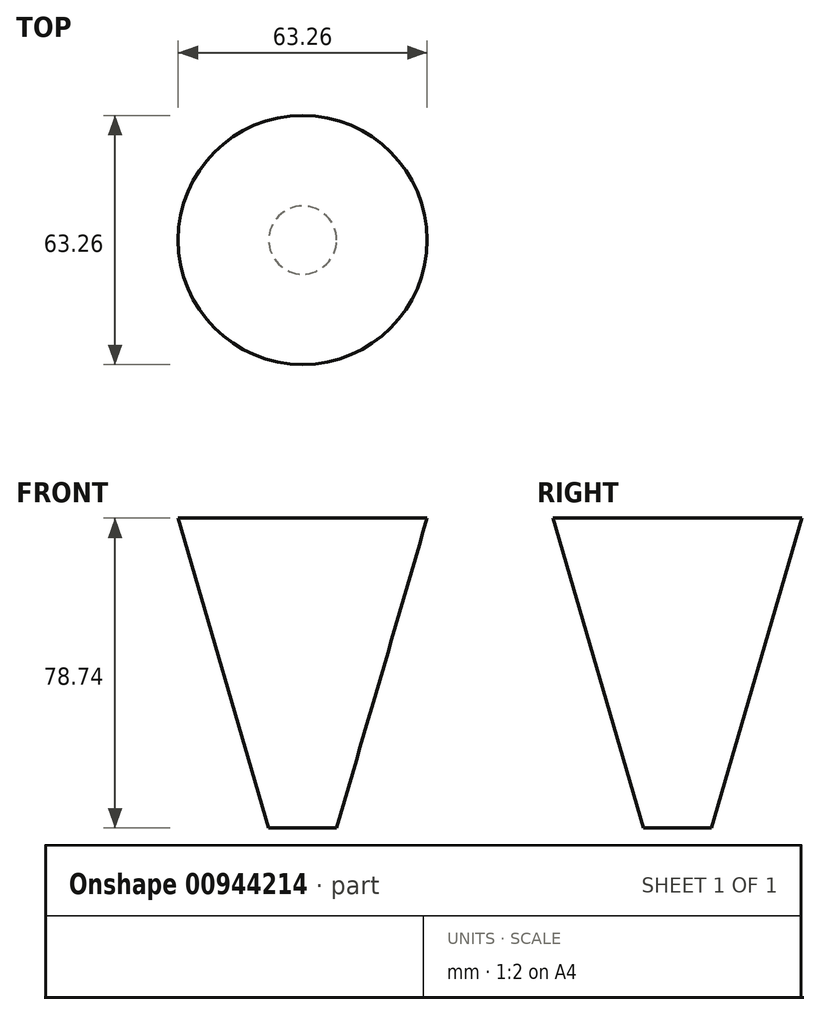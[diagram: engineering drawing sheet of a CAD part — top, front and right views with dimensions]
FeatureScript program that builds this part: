
annotation { "Feature Type Name" : "Feature", "Feature Type Description" : "" }
export const myFeature = defineFeature(function(context is Context, id is Id, definition is map)
    precondition{}
    {
        {
            var Q0;
            Q0=qCreatedBy(makeId("Top.planeOp"),FACE);
            var sketch = newSketch(context, id + "F0", { "sketchPlane" : qUnion([Q0])});
            skCircle(sketch, "E0", {"center": v(0, 0) * mm, "radius": 8.63 * mm});
            skSolve(sketch);
        }
        {
            var Q0;
            Q0=qCreatedBy(makeId("Top.planeOp"),FACE);
            cPlane(context, id + "F1", {"entities" : qUnion([Q0]), "cplaneType" : CPlaneType.OFFSET, "offset" : 78.74 * mm, "width" : 152.4 * mm, "height" : 152.4 * mm});
        }
        {
            var Q0;
            Q0=qCreatedBy(id+"F1.planeOp",FACE);
            var sketch = newSketch(context, id + "F2", { "sketchPlane" : qUnion([Q0])});
            skCircle(sketch, "E1", {"center": v(0, 0) * mm, "radius": 31.63 * mm});
            skSolve(sketch);
        }
        {
            var Q0;
            Q0=makeQuery(id+"F2.imprint","IMPRINT",FACE,{"disambiguationData":[TD([[makeQuery(id+"F2.imprint","IMPRINT",EDGE,{"derivedFrom":sQuery(id+"F2.wireOp",EDGE,"E1")}),1.0]])]});
            var Q1;
            Q1=makeQuery(id+"F0.imprint","IMPRINT",FACE,{"disambiguationData":[TD([[makeQuery(id+"F0.imprint","IMPRINT",EDGE,{"derivedFrom":sQuery(id+"F0.wireOp",EDGE,"E0")}),1.0]])]});
            loft(context, id + "F3", {"sheetProfilesArray" : [{ "sheetProfileEntities" : qUnion([Q0]) }, { "sheetProfileEntities" : qUnion([Q1]) }]});
        }
    });
